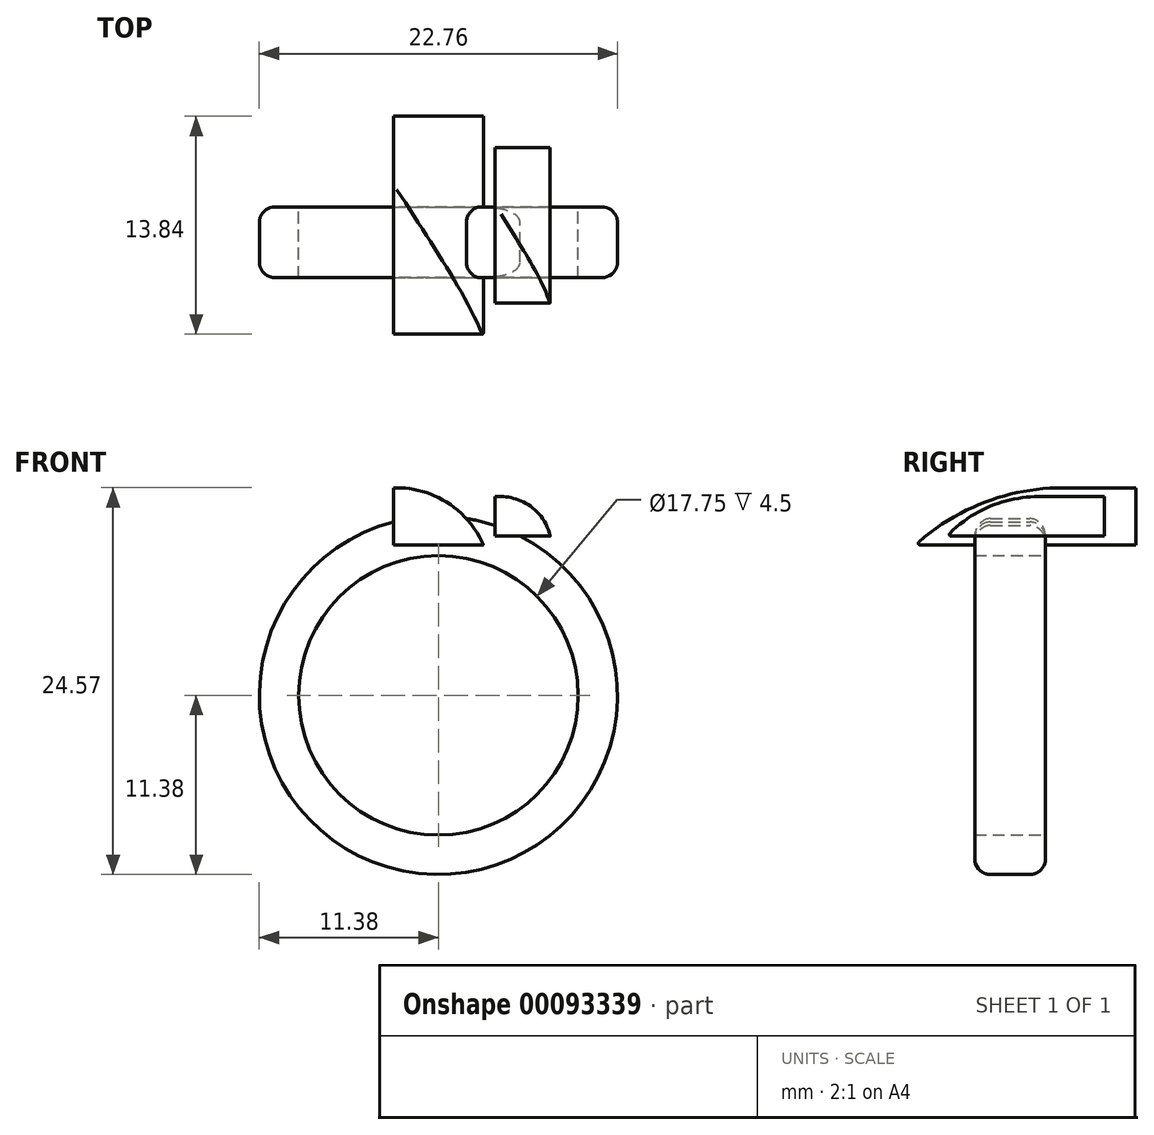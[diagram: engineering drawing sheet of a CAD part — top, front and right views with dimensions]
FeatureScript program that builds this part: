
annotation { "Feature Type Name" : "Feature", "Feature Type Description" : "" }
export const myFeature = defineFeature(function(context is Context, id is Id, definition is map)
    precondition{}
    {
        {
            var Q0;
            Q0=qCreatedBy(makeId("Front.planeOp"),FACE);
            var sketch = newSketch(context, id + "F0", { "sketchPlane" : qUnion([Q0])});
            skCircle(sketch, "E0", {"center": v(0, 0) * mm, "radius": 8.88 * mm});
            skCircle(sketch, "E1.0", {"center": v(0, 0) * mm, "radius": 11.38 * mm});
            skPoint(sketch, "E2", {"position": v(0, 11.38) * mm});
            skPoint(sketch, "E3", {"position": v(11.38, 0) * mm});
            skPoint(sketch, "E4", {"position": v(-11.38, 0) * mm});
            skLineSegment(sketch, "E5", {"start": v(11.38, 0) * mm, "end": v(11.38, 11.37) * mm});
            skLineSegment(sketch, "E6", {"start": v(11.38, 11.38) * mm, "end": v(0, 11.38) * mm});
            skLineSegment(sketch, "E7.MirrorCS", {"start": v(-11.38, 11.37) * mm, "end": v(0, 11.38) * mm});
            skLineSegment(sketch, "E8.MirrorCS", {"start": v(-11.38, 0) * mm, "end": v(-11.38, 11.37) * mm});
            skLineSegment(sketch, "E9.bottom", {"start": v(-2.85, 9.56) * mm, "end": v(2.85, 9.56) * mm});
            skLineSegment(sketch, "E9.top", {"start": v(-2.85, 13.19) * mm, "end": v(2.85, 13.19) * mm});
            skLineSegment(sketch, "E9.left", {"start": v(-2.85, 9.56) * mm, "end": v(-2.85, 13.19) * mm});
            skLineSegment(sketch, "E9.right", {"start": v(2.85, 9.56) * mm, "end": v(2.85, 13.19) * mm});
            skLineSegment(sketch, "E10.bottom", {"start": v(7.1, 10.13) * mm, "end": v(3.6, 10.13) * mm});
            skLineSegment(sketch, "E10.top", {"start": v(7.1, 12.63) * mm, "end": v(3.6, 12.63) * mm});
            skLineSegment(sketch, "E10.left", {"start": v(7.1, 10.13) * mm, "end": v(7.1, 12.63) * mm});
            skLineSegment(sketch, "E10.right", {"start": v(3.6, 10.13) * mm, "end": v(3.6, 12.63) * mm});
            skPoint(sketch, "E10.middle", {"position": v(5.35, 11.38) * mm});
            skPoint(sketch, "E11", {"position": v(5.69, 11.38) * mm});
            skSolve(sketch);
        }
        {
            var Q0;
            Q0=makeQuery(id+"F0.imprint","IMPRINT",FACE,{"disambiguationData":[TD([[makeQuery(id+"F0.imprint","IMPRINT",EDGE,{"derivedFrom":sQuery(id+"F0.wireOp",EDGE,"E0")}),-1.0]])]});
            extrude(context, id + "F1", {"entities" : qUnion([Q0]), "depth" : 2.25 * mm, "hasSecondDirection" : true, "secondDirectionOppositeDirection" : true, "secondDirectionDepth" : 2.25 * mm});
        }
        {
            var Q0;
            Q0=makeQuery(id+"F1.opExtrude","CAP_EDGE",EDGE,{"disambiguationData":[OSD([sQuery(id+"F0.wireOp",EDGE,"E1.0")])],"isStart":false});
            var Q1;
            Q1=makeQuery(id+"F1.opExtrude","CAP_EDGE",EDGE,{"disambiguationData":[OSD([sQuery(id+"F0.wireOp",EDGE,"E1.0")])],"isStart":true});
            var Q2;
            Q2=makeQuery(id+"F1.opExtrude","CAP_EDGE",EDGE,{"disambiguationData":[OSD([sQuery(id+"F0.wireOp",EDGE,"E5")])],"isStart":false});
            var Q3;
            Q3=makeQuery(id+"F1.opExtrude","CAP_EDGE",EDGE,{"disambiguationData":[OSD([sQuery(id+"F0.wireOp",EDGE,"E5")])],"isStart":true});
            fillet(context, id + "F2", {"entities" : qUnion([Q0, Q1, Q2, Q3]), "radius" : 1 * mm, "tangentPropagation" : true, "allowEdgeOverflow" : false});
        }
        {
            var Q0;
            {var subQ1=sQuery(id+"F0.wireOp",EDGE,"E9.top");Q0=makeQuery(id+"F0.imprint","IMPRINT",FACE,{"disambiguationData":[TD([[makeQuery(id+"F0.imprint","IMPRINT",EDGE,{"derivedFrom":subQ1}),-1.0]])]});}
            var Q1;
            {var subQ0=sQuery(id+"F0.wireOp",EDGE,"E7.MirrorCS");var subQ3=sQuery(id+"F0.wireOp",EDGE,"E9.left");var subQ5=makeQuery(id+"F0.imprint","INTERSECT",VERTEX,{"derivedFrom":[subQ0,subQ3]});Q1=makeQuery(id+"F0.imprint","IMPRINT",FACE,{"disambiguationData":[TD([[makeQuery(id+"F0.imprint","IMPRINT",EDGE,{"disambiguationData":[TD([[subQ5,1.0]])],"derivedFrom":subQ3}),-1.0]])]});}
            var Q2;
            {var subQ1=sQuery(id+"F0.wireOp",EDGE,"E9.bottom");Q2=makeQuery(id+"F0.imprint","IMPRINT",FACE,{"disambiguationData":[TD([[makeQuery(id+"F0.imprint","IMPRINT",EDGE,{"derivedFrom":subQ1}),1.0]])]});}
            var Q3;
            {var subQ0=sQuery(id+"F0.wireOp",EDGE,"E6");var subQ3=sQuery(id+"F0.wireOp",EDGE,"E9.right");var subQ5=makeQuery(id+"F0.imprint","INTERSECT",VERTEX,{"derivedFrom":[subQ0,subQ3]});Q3=makeQuery(id+"F0.imprint","IMPRINT",FACE,{"disambiguationData":[TD([[makeQuery(id+"F0.imprint","IMPRINT",EDGE,{"disambiguationData":[TD([[subQ5,1.0]])],"derivedFrom":subQ3}),1.0]])]});}
            extrude(context, id + "F3", {"entities" : qUnion([Q0, Q1, Q2, Q3]), "operationType" : NewBodyOperationType.ADD, "depth" : 6 * mm, "hasSecondDirection" : true, "secondDirectionOppositeDirection" : true, "secondDirectionDepth" : 8 * mm});
        }
        {
            var Q0;
            {var subQ1=sQuery(id+"F0.wireOp",EDGE,"E10.bottom");var subQ5=sQuery(id+"F0.wireOp",EDGE,"E1.0");var subQ6=makeQuery(id+"F0.imprint","INTERSECT",VERTEX,{"derivedFrom":[subQ5,subQ1]});Q0=makeQuery(id+"F0.imprint","IMPRINT",FACE,{"disambiguationData":[TD([[makeQuery(id+"F0.imprint","IMPRINT",EDGE,{"disambiguationData":[TD([[subQ6,-1.0]])],"derivedFrom":subQ5}),-1.0]])]});}
            var Q1;
            {var subQ0=sQuery(id+"F0.wireOp",EDGE,"E10.bottom");var subQ1=sQuery(id+"F0.wireOp",EDGE,"E1.0");var subQ2=makeQuery(id+"F0.imprint","INTERSECT",VERTEX,{"derivedFrom":[subQ1,subQ0]});Q1=makeQuery(id+"F0.imprint","IMPRINT",FACE,{"disambiguationData":[TD([[makeQuery(id+"F0.imprint","IMPRINT",EDGE,{"disambiguationData":[TD([[subQ2,-1.0]])],"derivedFrom":subQ1}),1.0]])]});}
            var Q2;
            {var subQ5=sQuery(id+"F0.wireOp",EDGE,"E10.top");Q2=makeQuery(id+"F0.imprint","IMPRINT",FACE,{"disambiguationData":[TD([[makeQuery(id+"F0.imprint","IMPRINT",EDGE,{"derivedFrom":subQ5}),1.0]])]});}
            extrude(context, id + "F4", {"entities" : qUnion([Q0, Q1, Q2]), "operationType" : NewBodyOperationType.ADD, "depth" : 4 * mm, "hasSecondDirection" : true, "secondDirectionOppositeDirection" : true, "secondDirectionDepth" : 6 * mm});
        }
        {
            var Q0;
            Q0=makeQuery(id+"F3.opExtrude","SWEPT_EDGE",EDGE,{"disambiguationData":[OSD([sQuery(id+"F0.wireOp",EDGE,"E9.top"),sQuery(id+"F0.wireOp",EDGE,"E9.right")])]});
            fillet(context, id + "F5", {"entities" : qUnion([Q0]), "radius" : 5.98 * mm, "tangentPropagation" : true, "allowEdgeOverflow" : false});
        }
        {
            var Q0;
            {var subQ0=sQuery(id+"F0.wireOp",EDGE,"E9.right");var subQ1=sQuery(id+"F0.wireOp",EDGE,"E9.top");Q0=makeQuery(id+"F5.opFillet","BLEND_EDGE",EDGE,{"blendedFrom":[makeQuery(id+"F3.opExtrude","SWEPT_EDGE",EDGE,{"disambiguationData":[OSD([subQ1,subQ0])]}),makeQuery(id+"F3.opExtrude","CAP_FACE",FACE,{"disambiguationData":[OSD([sQuery(id+"F0.wireOp",EDGE,"E9.bottom"),subQ1,sQuery(id+"F0.wireOp",EDGE,"E9.left"),subQ0])],"isStart":false})],"blendedInto":[makeQuery(id+"F3.opExtrude","CAP_FACE",FACE,{"disambiguationData":[OSD([sQuery(id+"F0.wireOp",EDGE,"E9.bottom"),subQ1,sQuery(id+"F0.wireOp",EDGE,"E9.left"),subQ0])],"isStart":false})]});}
            fillet(context, id + "F6", {"entities" : qUnion([Q0]), "radius" : 13.86 * mm, "tangentPropagation" : true, "allowEdgeOverflow" : false});
        }
        {
            var Q0;
            Q0=makeQuery(id+"F4.opExtrude","SWEPT_EDGE",EDGE,{"disambiguationData":[OSD([sQuery(id+"F0.wireOp",EDGE,"E10.top"),sQuery(id+"F0.wireOp",EDGE,"E10.left")])]});
            fillet(context, id + "F7", {"entities" : qUnion([Q0]), "radius" : 3.2 * mm, "tangentPropagation" : true, "allowEdgeOverflow" : false});
        }
        {
            var Q0;
            {var subQ0=sQuery(id+"F0.wireOp",EDGE,"E10.left");var subQ1=sQuery(id+"F0.wireOp",EDGE,"E10.top");Q0=makeQuery(id+"F7.opFillet","BLEND_EDGE",EDGE,{"blendedFrom":[makeQuery(id+"F4.opExtrude","SWEPT_EDGE",EDGE,{"disambiguationData":[OSD([subQ1,subQ0])]}),makeQuery(id+"F4.opExtrude","CAP_FACE",FACE,{"disambiguationData":[OSD([sQuery(id+"F0.wireOp",EDGE,"E10.bottom"),subQ1,subQ0,sQuery(id+"F0.wireOp",EDGE,"E10.right")])],"isStart":false})],"blendedInto":[makeQuery(id+"F4.opExtrude","CAP_FACE",FACE,{"disambiguationData":[OSD([sQuery(id+"F0.wireOp",EDGE,"E10.bottom"),subQ1,subQ0,sQuery(id+"F0.wireOp",EDGE,"E10.right")])],"isStart":false})]});}
            fillet(context, id + "F8", {"entities" : qUnion([Q0]), "radius" : 7.96 * mm, "tangentPropagation" : true, "allowEdgeOverflow" : false});
        }
        {
            var Q0;
            Q0=makeQuery(id+"F8.opFillet","BLEND_EDGE",EDGE,{"blendedFrom":[makeQuery(id+"F4.opExtrude","CAP_EDGE",EDGE,{"disambiguationData":[OSD([sQuery(id+"F0.wireOp",EDGE,"E10.top")])],"isStart":false}),makeQuery(id+"F4.opExtrude","SWEPT_FACE",FACE,{"disambiguationData":[OSD([sQuery(id+"F0.wireOp",EDGE,"E10.bottom")])]})],"blendedInto":[makeQuery(id+"F4.opExtrude","SWEPT_FACE",FACE,{"disambiguationData":[OSD([sQuery(id+"F0.wireOp",EDGE,"E10.bottom")])]})]});
            var Q1;
            {var subQ0=sQuery(id+"F0.wireOp",EDGE,"E9.right");var subQ1=sQuery(id+"F0.wireOp",EDGE,"E9.left");var subQ2=sQuery(id+"F0.wireOp",EDGE,"E9.bottom");var subQ3=sQuery(id+"F0.wireOp",EDGE,"E9.top");Q1=makeQuery(id+"F6.opFillet","BLEND_EDGE",EDGE,{"blendedFrom":[makeQuery(id+"F3.opExtrude","CAP_EDGE",EDGE,{"disambiguationData":[OSD([subQ3])],"isStart":false}),makeQuery(id+"F3.boolean.opBoolean","SPLIT",FACE,{"disambiguationData":[TD([makeQuery(id+"F3.opExtrude","CAP_FACE",FACE,{"disambiguationData":[OSD([subQ2,subQ3,subQ1,subQ0])],"isStart":false})])],"derivedFrom":makeQuery(id+"F3.opExtrude","SWEPT_FACE",FACE,{"disambiguationData":[OSD([subQ2])]})})],"blendedInto":[makeQuery(id+"F3.boolean.opBoolean","SPLIT",FACE,{"disambiguationData":[TD([makeQuery(id+"F3.opExtrude","CAP_FACE",FACE,{"disambiguationData":[OSD([subQ2,subQ3,subQ1,subQ0])],"isStart":false})])],"derivedFrom":makeQuery(id+"F3.opExtrude","SWEPT_FACE",FACE,{"disambiguationData":[OSD([subQ2])]})})]});}
            fillet(context, id + "F9", {"entities" : qUnion([Q0, Q1]), "radius" : .1 * mm, "tangentPropagation" : true, "allowEdgeOverflow" : false});
        }
    });
